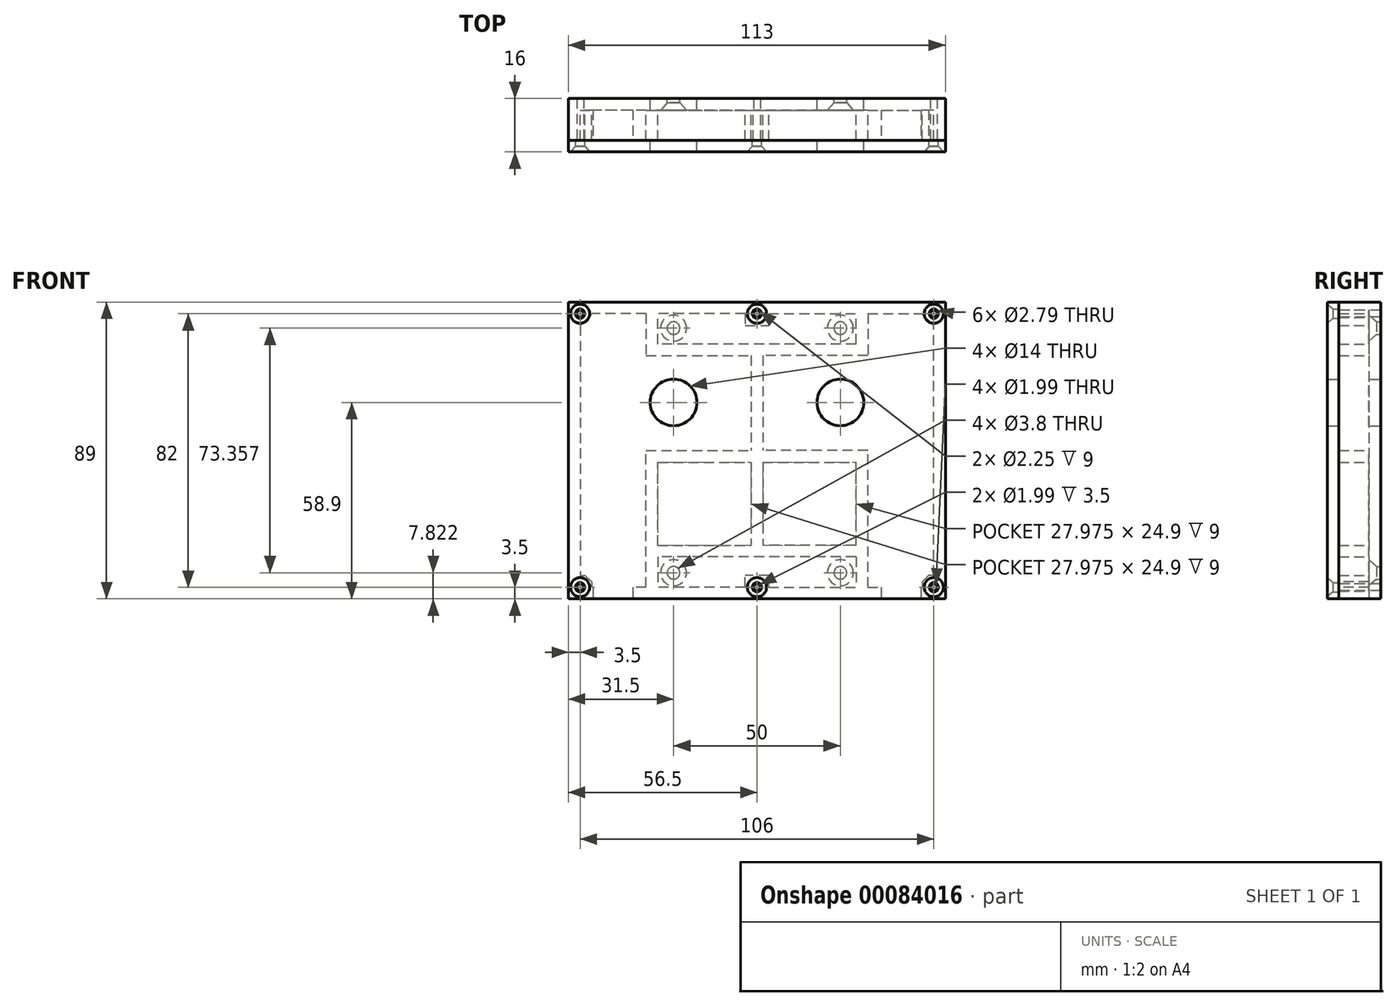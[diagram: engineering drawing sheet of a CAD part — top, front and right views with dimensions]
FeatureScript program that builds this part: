
annotation { "Feature Type Name" : "Feature", "Feature Type Description" : "" }
export const myFeature = defineFeature(function(context is Context, id is Id, definition is map)
    precondition{}
    {
        {
            var Q0;
            Q0=qCreatedBy(makeId("Front.planeOp"),FACE);
            var sketch = newSketch(context, id + "F0", { "sketchPlane" : qUnion([Q0])});
            skLineSegment(sketch, "E0.0", {"start": v(-53, 0) * mm, "end": v(-53, 37.41) * mm});
            skLineSegment(sketch, "E1.trimOffspring", {"start": v(-29.73, 31.9) * mm, "end": v(-29.73, 41) * mm});
            skLineSegment(sketch, "E2.0", {"start": v(0, 31.9) * mm, "end": v(-29.73, 31.9) * mm});
            skLineSegment(sketch, "E3.trimOffspring", {"start": v(-33.23, 41) * mm, "end": v(-49.5, 41) * mm});
            skLineSegment(sketch, "E4.trimOffspring", {"start": v(-3.5, 41) * mm, "end": v(-29.73, 41) * mm});
            skLineSegment(sketch, "E5.MirrorCS", {"start": v(-3.5, 41) * mm, "end": v(-3.5, 37.5) * mm});
            skLineSegment(sketch, "E6", {"start": v(-3.5, 37.5) * mm, "end": v(0, 37.5) * mm});
            skCircle(sketch, "E7", {"center": v(-25, 14.4) * mm, "radius": 7 * mm});
            skCircle(sketch, "E8", {"center": v(-53, 41) * mm, "radius": 0.5 * mm});
            skLineSegment(sketch, "E9", {"start": v(-56.5, 44.5) * mm, "end": v(-56.5, 0) * mm});
            skLineSegment(sketch, "E10", {"start": v(-56.5, 44.5) * mm, "end": v(0, 44.5) * mm});
            skLineSegment(sketch, "E11", {"start": v(-53, 37.41) * mm, "end": v(-49.5, 41) * mm});
            skLineSegment(sketch, "E12", {"start": v(0, 89.77) * mm, "end": v(0, -70.35) * mm, "construction": true});
            skLineSegment(sketch, "E13", {"start": v(-110.4, 0) * mm, "end": v(109.76, 0) * mm, "construction": true});
            skLineSegment(sketch, "E14", {"start": v(-33.23, 28.4) * mm, "end": v(0, 28.4) * mm});
            skLineSegment(sketch, "E15.MirrorCS", {"start": v(56.5, 44.5) * mm, "end": v(0, 44.5) * mm});
            skLineSegment(sketch, "E16.MirrorCS", {"start": v(56.5, 44.5) * mm, "end": v(56.5, 0) * mm});
            skLineSegment(sketch, "E17.MirrorCS", {"start": v(-56.5, -44.5) * mm, "end": v(-56.5, 0) * mm});
            skLineSegment(sketch, "E18.MirrorCS", {"start": v(-56.5, -44.5) * mm, "end": v(0, -44.5) * mm});
            skLineSegment(sketch, "E19.MirrorCS", {"start": v(56.5, -44.5) * mm, "end": v(0, -44.5) * mm});
            skLineSegment(sketch, "E20.MirrorCS", {"start": v(56.5, -44.5) * mm, "end": v(56.5, 0) * mm});
            skLineSegment(sketch, "E21.MirrorCS", {"start": v(33.23, 28.4) * mm, "end": v(0, 28.4) * mm});
            skLineSegment(sketch, "E22.MirrorCS", {"start": v(0, 31.9) * mm, "end": v(29.73, 31.9) * mm});
            skLineSegment(sketch, "E23.MirrorCS", {"start": v(33.23, 41) * mm, "end": v(33.23, 28.4) * mm});
            skLineSegment(sketch, "E24.MirrorCS", {"start": v(29.73, 31.9) * mm, "end": v(29.73, 41) * mm});
            skLineSegment(sketch, "E25.MirrorCS", {"start": v(3.5, 41) * mm, "end": v(29.73, 41) * mm});
            skLineSegment(sketch, "E26.MirrorCS", {"start": v(33.23, 41) * mm, "end": v(49.5, 41) * mm});
            skLineSegment(sketch, "E27.MirrorCS", {"start": v(53, 37.41) * mm, "end": v(49.5, 41) * mm});
            skLineSegment(sketch, "E28.MirrorCS", {"start": v(53, 0) * mm, "end": v(53, 37.41) * mm});
            skCircle(sketch, "E29.MirrorC", {"center": v(25, 14.4) * mm, "radius": 7 * mm});
            skCircle(sketch, "E30.MirrorC", {"center": v(53, 41) * mm, "radius": 0.5 * mm});
            skLineSegment(sketch, "E31.MirrorCS", {"start": v(53, 0) * mm, "end": v(53, -37.41) * mm});
            skCircle(sketch, "E32.MirrorC", {"center": v(53, -41) * mm, "radius": 0.5 * mm});
            skLineSegment(sketch, "E33.MirrorCS", {"start": v(33.23, -41) * mm, "end": v(49.5, -41) * mm});
            skLineSegment(sketch, "E34.MirrorCS", {"start": v(29.73, -28.4) * mm, "end": v(0, -28.4) * mm});
            skLineSegment(sketch, "E35.MirrorCS", {"start": v(0, -31.9) * mm, "end": v(29.73, -31.9) * mm});
            skLineSegment(sketch, "E36.MirrorCS", {"start": v(29.73, -31.9) * mm, "end": v(29.73, -41) * mm});
            skLineSegment(sketch, "E37.MirrorCS", {"start": v(3.5, -41) * mm, "end": v(29.73, -41) * mm});
            skLineSegment(sketch, "E38.MirrorCS", {"start": v(3.5, 41) * mm, "end": v(3.5, 37.5) * mm});
            skLineSegment(sketch, "E39.MirrorCS", {"start": v(3.5, 37.5) * mm, "end": v(0, 37.5) * mm});
            skLineSegment(sketch, "E40.MirrorCS", {"start": v(3.5, -41) * mm, "end": v(3.5, -37.5) * mm});
            skLineSegment(sketch, "E41.MirrorCS", {"start": v(3.5, -37.5) * mm, "end": v(0, -37.5) * mm});
            skLineSegment(sketch, "E42.MirrorCS", {"start": v(-3.5, -37.5) * mm, "end": v(0, -37.5) * mm});
            skLineSegment(sketch, "E43.MirrorCS", {"start": v(-3.5, -41) * mm, "end": v(-3.5, -37.5) * mm});
            skLineSegment(sketch, "E44.MirrorCS", {"start": v(-3.5, -41) * mm, "end": v(-29.73, -41) * mm});
            skLineSegment(sketch, "E45.MirrorCS", {"start": v(-29.73, -31.9) * mm, "end": v(-29.73, -41) * mm});
            skLineSegment(sketch, "E46.MirrorCS", {"start": v(0, -31.9) * mm, "end": v(-29.73, -31.9) * mm});
            skLineSegment(sketch, "E47.MirrorCS", {"start": v(-29.73, -28.4) * mm, "end": v(0, -28.4) * mm});
            skLineSegment(sketch, "E48.MirrorCS", {"start": v(-33.23, -41) * mm, "end": v(-49.5, -41) * mm});
            skLineSegment(sketch, "E49.MirrorCS", {"start": v(-53, 0) * mm, "end": v(-53, -37.41) * mm});
            skCircle(sketch, "E50.MirrorC", {"center": v(-53, -41) * mm, "radius": 0.5 * mm});
            skCircle(sketch, "E51", {"center": v(0, 41) * mm, "radius": 1.13 * mm});
            skCircle(sketch, "E52.MirrorC", {"center": v(0, -41) * mm, "radius": 1.13 * mm});
            skLineSegment(sketch, "E53", {"start": v(-1.75, 28.4) * mm, "end": v(-1.75, -28.4) * mm});
            skLineSegment(sketch, "E54.MirrorCS", {"start": v(1.75, 28.4) * mm, "end": v(1.75, -28.4) * mm});
            skLineSegment(sketch, "E55.left", {"start": v(-29.73, -28.4) * mm, "end": v(-29.73, -3.5) * mm});
            skLineSegment(sketch, "E55.right", {"start": v(-33.23, -41) * mm, "end": v(-33.23, 0) * mm});
            skLineSegment(sketch, "E56.MirrorCS", {"start": v(29.73, -28.4) * mm, "end": v(29.73, -3.5) * mm});
            skLineSegment(sketch, "E57.top", {"start": v(-29.73, -3.5) * mm, "end": v(29.73, -3.5) * mm});
            skLineSegment(sketch, "E58", {"start": v(-33.23, 41) * mm, "end": v(-33.23, 28.4) * mm});
            skLineSegment(sketch, "E59", {"start": v(-53, -37.41) * mm, "end": v(-49.5, -37.41) * mm});
            skLineSegment(sketch, "E60", {"start": v(-49.5, -37.41) * mm, "end": v(-49.5, -41) * mm});
            skLineSegment(sketch, "E61.MirrorCS", {"start": v(53, -37.41) * mm, "end": v(49.5, -37.41) * mm});
            skLineSegment(sketch, "E62.MirrorCS", {"start": v(49.5, -37.41) * mm, "end": v(49.5, -41) * mm});
            skCircle(sketch, "E63", {"center": v(-25, 36.68) * mm, "radius": 0.5 * mm});
            skCircle(sketch, "E64.MirrorC", {"center": v(25, 36.68) * mm, "radius": 0.5 * mm});
            skCircle(sketch, "E65.MirrorC", {"center": v(-25, -36.68) * mm, "radius": 0.5 * mm});
            skLineSegment(sketch, "E66.MirrorCS", {"start": v(33.23, -41) * mm, "end": v(33.23, 0) * mm});
            skLineSegment(sketch, "E67", {"start": v(-33.23, 0) * mm, "end": v(0, 0) * mm});
            skLineSegment(sketch, "E68.MirrorCS", {"start": v(33.23, 0) * mm, "end": v(0, 0) * mm});
            skCircle(sketch, "E69.MirrorC", {"center": v(25, -36.68) * mm, "radius": 0.5 * mm});
            skSolve(sketch);
        }
        {
            var Q0;
            {var subQ17=sQuery(id+"F0.wireOp",EDGE,"E0.0");Q0=makeQuery(id+"F0.imprint","IMPRINT",FACE,{"disambiguationData":[TD([[makeQuery(id+"F0.imprint","IMPRINT",EDGE,{"derivedFrom":subQ17}),1.0]])]});}
            var Q1;
            {var subQ1=sQuery(id+"F0.wireOp",EDGE,"E21.MirrorCS");var subQ6=sQuery(id+"F0.wireOp",EDGE,"E14");var subQ9=makeQuery(id+"F0.imprint","INTERSECT",VERTEX,{"derivedFrom":[subQ6,subQ1]});Q1=makeQuery(id+"F0.imprint","IMPRINT",FACE,{"disambiguationData":[TD([[makeQuery(id+"F0.imprint","IMPRINT",EDGE,{"disambiguationData":[TD([[subQ9,1.0]])],"derivedFrom":subQ6}),-1.0]])]});}
            var Q2;
            {var subQ0=sQuery(id+"F0.wireOp",EDGE,"E57.bottom");var subQ1=sQuery(id+"F0.wireOp",EDGE,"E53");var subQ2=makeQuery(id+"F0.imprint","INTERSECT",VERTEX,{"derivedFrom":[subQ1,subQ0]});Q2=makeQuery(id+"F0.imprint","IMPRINT",FACE,{"disambiguationData":[TD([[makeQuery(id+"F0.imprint","IMPRINT",EDGE,{"disambiguationData":[TD([[subQ2,-1.0]])],"derivedFrom":subQ1}),1.0]])]});}
            var Q3;
            {var subQ1=sQuery(id+"F0.wireOp",EDGE,"E47.MirrorCS");var subQ6=sQuery(id+"F0.wireOp",EDGE,"E34.MirrorCS");var subQ9=makeQuery(id+"F0.imprint","INTERSECT",VERTEX,{"derivedFrom":[subQ6,subQ1]});Q3=makeQuery(id+"F0.imprint","IMPRINT",FACE,{"disambiguationData":[TD([[makeQuery(id+"F0.imprint","IMPRINT",EDGE,{"disambiguationData":[TD([[subQ9,1.0]])],"derivedFrom":subQ6}),-1.0]])]});}
            extrude(context, id + "F1", {"entities" : qUnion([Q0, Q1, Q2, Q3]), "depth" : 12.5 * mm});
        }
        {
            var Q0;
            {var subQ3=sQuery(id+"F0.wireOp",EDGE,"E0.0");Q0=makeQuery(id+"F0.imprint","IMPRINT",FACE,{"disambiguationData":[TD([[makeQuery(id+"F0.imprint","IMPRINT",EDGE,{"derivedFrom":subQ3}),-1.0]])]});}
            var Q1;
            Q1=makeQuery(id+"F0.imprint","IMPRINT",FACE,{"disambiguationData":[TD([[makeQuery(id+"F0.imprint","IMPRINT",EDGE,{"derivedFrom":sQuery(id+"F0.wireOp",EDGE,"E1.trimOffspring")}),-1.0]])]});
            var Q2;
            {var subQ8=sQuery(id+"F0.wireOp",EDGE,"E23.MirrorCS");Q2=makeQuery(id+"F0.imprint","IMPRINT",FACE,{"disambiguationData":[TD([[makeQuery(id+"F0.imprint","IMPRINT",EDGE,{"derivedFrom":subQ8}),1.0]])]});}
            var Q3;
            {var subQ0=sQuery(id+"F0.wireOp",EDGE,"E56.MirrorCS");Q3=makeQuery(id+"F0.imprint","IMPRINT",FACE,{"disambiguationData":[TD([[makeQuery(id+"F0.imprint","IMPRINT",EDGE,{"derivedFrom":subQ0}),1.0]])]});}
            var Q4;
            Q4=makeQuery(id+"F0.imprint","IMPRINT",FACE,{"disambiguationData":[TD([[makeQuery(id+"F0.imprint","IMPRINT",EDGE,{"derivedFrom":sQuery(id+"F0.wireOp",EDGE,"E35.MirrorCS")}),-1.0]])]});
            var Q5;
            {var subQ0=sQuery(id+"F0.wireOp",EDGE,"E55.left");Q5=makeQuery(id+"F0.imprint","IMPRINT",FACE,{"disambiguationData":[TD([[makeQuery(id+"F0.imprint","IMPRINT",EDGE,{"derivedFrom":subQ0}),-1.0]])]});}
            extrude(context, id + "F2", {"entities" : qUnion([Q0, Q1, Q2, Q3, Q4, Q5]), "operationType" : NewBodyOperationType.ADD, "depth" : 3.5 * mm});
        }
        {
            var Q0;
            Q0=makeQuery(id+"F1.opExtrude","SWEPT_FACE",FACE,{"disambiguationData":[OSD([sQuery(id+"F0.wireOp",EDGE,"E18.MirrorCS"),sQuery(id+"F0.wireOp",EDGE,"E19.MirrorCS")])]});
            var sketch = newSketch(context, id + "F3", { "sketchPlane" : qUnion([Q0])});
            skLineSegment(sketch, "E70.bottom", {"start": v(-37.25, 3.5) * mm, "end": v(-49.15, 3.5) * mm});
            skLineSegment(sketch, "E70.left", {"start": v(-37.25, 3.5) * mm, "end": v(-37.25, 12.5) * mm});
            skLineSegment(sketch, "E70.right", {"start": v(-49.15, 3.5) * mm, "end": v(-49.15, 12.5) * mm});
            skPoint(sketch, "E70.middle", {"position": v(-43.2, 6.25) * mm});
            skPoint(sketch, "E70.middle.positionSnap0", {"position": v(-56.5, 6.25) * mm});
            skPoint(sketch, "E70.centerSnap0", {"position": v(-56.5, 6.25) * mm});
            skLineSegment(sketch, "E71", {"start": v(-49.15, 12.5) * mm, "end": v(-37.25, 12.5) * mm});
            skLineSegment(sketch, "E72.MirrorCS", {"start": v(49.15, 12.5) * mm, "end": v(37.25, 12.5) * mm});
            skLineSegment(sketch, "E73.MirrorCS", {"start": v(37.25, 3.5) * mm, "end": v(37.25, 12.5) * mm});
            skLineSegment(sketch, "E74.MirrorCS", {"start": v(49.15, 3.5) * mm, "end": v(49.15, 12.5) * mm});
            skLineSegment(sketch, "E75.MirrorCS", {"start": v(37.25, 3.5) * mm, "end": v(49.15, 3.5) * mm});
            skSolve(sketch);
        }
        {
            var Q0;
            Q0=makeQuery(id+"F3.imprint","IMPRINT",FACE,{"disambiguationData":[TD([[makeQuery(id+"F3.imprint","IMPRINT",EDGE,{"derivedFrom":sQuery(id+"F3.wireOp",EDGE,"E70.bottom")}),-1.0]])]});
            var Q1;
            Q1=makeQuery(id+"F3.imprint","IMPRINT",FACE,{"disambiguationData":[TD([[makeQuery(id+"F3.imprint","IMPRINT",EDGE,{"derivedFrom":sQuery(id+"F3.wireOp",EDGE,"E72.MirrorCS")}),-1.0]])]});
            extrude(context, id + "F4", {"entities" : qUnion([Q0, Q1]), "operationType" : NewBodyOperationType.REMOVE, "oppositeDirection" : true, "depth" : 19.49 * mm});
        }
        {
            var Q0;
            Q0=qCreatedBy(makeId("Front.planeOp"),FACE);
            var sketch = newSketch(context, id + "F5", { "sketchPlane" : qUnion([Q0])});
            skLineSegment(sketch, "E76.0.2", {"start": v(49.15, -44.5) * mm, "end": v(56.5, -44.5) * mm});
            skLineSegment(sketch, "E76.0.3", {"start": v(56.5, -44.5) * mm, "end": v(56.5, 44.5) * mm});
            skLineSegment(sketch, "E76.0.4", {"start": v(56.5, 44.5) * mm, "end": v(-56.5, 44.5) * mm});
            skLineSegment(sketch, "E76.0.5", {"start": v(-56.5, 44.5) * mm, "end": v(-56.5, -44.5) * mm});
            skLineSegment(sketch, "E76.0.6", {"start": v(-56.5, -44.5) * mm, "end": v(-49.15, -44.5) * mm});
            skLineSegment(sketch, "E76.0.20", {"start": v(-37.25, -44.5) * mm, "end": v(37.25, -44.5) * mm});
            skCircle(sketch, "E77.0", {"center": v(-53, 41) * mm, "radius": 0.5 * mm});
            skCircle(sketch, "E78.0", {"center": v(0, 41) * mm, "radius": 1.13 * mm});
            skCircle(sketch, "E79.0", {"center": v(53, 41) * mm, "radius": 0.5 * mm});
            skCircle(sketch, "E80.0", {"center": v(53, -41) * mm, "radius": 0.5 * mm});
            skCircle(sketch, "E81.0", {"center": v(0, -41) * mm, "radius": 1.13 * mm});
            skCircle(sketch, "E82.0", {"center": v(-53, -41) * mm, "radius": 0.5 * mm});
            skLineSegment(sketch, "E83", {"start": v(-49.15, -44.5) * mm, "end": v(-37.25, -44.5) * mm});
            skLineSegment(sketch, "E84", {"start": v(37.25, -44.5) * mm, "end": v(49.15, -44.5) * mm});
            skCircle(sketch, "E85.0", {"center": v(-25, 14.4) * mm, "radius": 7 * mm});
            skCircle(sketch, "E86.0", {"center": v(25, 14.4) * mm, "radius": 7 * mm});
            skSolve(sketch);
        }
        {
            var Q0;
            Q0 = qSketchRegion(id + "F5", true);
            extrude(context, id + "F6", {"entities" : qUnion([Q0]), "depth" : 3.5 * mm});
        }
        {
            var Q0;
            Q0=makeQuery(id+"F6.opExtrude","CAP_FACE",FACE,{"disambiguationData":[OSD([sQuery(id+"F5.wireOp",EDGE,"E76.0.2"),sQuery(id+"F5.wireOp",EDGE,"E76.0.3"),sQuery(id+"F5.wireOp",EDGE,"E76.0.4"),sQuery(id+"F5.wireOp",EDGE,"E76.0.5"),sQuery(id+"F5.wireOp",EDGE,"E76.0.6"),sQuery(id+"F5.wireOp",EDGE,"E76.0.20"),sQuery(id+"F5.wireOp",EDGE,"E77.0"),sQuery(id+"F5.wireOp",EDGE,"E78.0"),sQuery(id+"F5.wireOp",EDGE,"E79.0"),sQuery(id+"F5.wireOp",EDGE,"E80.0"),sQuery(id+"F5.wireOp",EDGE,"E81.0"),sQuery(id+"F5.wireOp",EDGE,"E82.0"),sQuery(id+"F5.wireOp",EDGE,"E83"),sQuery(id+"F5.wireOp",EDGE,"E84"),sQuery(id+"F5.wireOp",EDGE,"E85.0"),sQuery(id+"F5.wireOp",EDGE,"E86.0")])],"isStart":false});
            var sketch = newSketch(context, id + "F7", { "sketchPlane" : qUnion([Q0])});
            skCircle(sketch, "E87.0", {"center": v(-53, 41) * mm, "radius": 0.5 * mm});
            skCircle(sketch, "E88.0", {"center": v(0, 41) * mm, "radius": 1.13 * mm});
            skCircle(sketch, "E89.0", {"center": v(53, 41) * mm, "radius": 0.5 * mm});
            skCircle(sketch, "E90.0", {"center": v(53, -41) * mm, "radius": 0.5 * mm});
            skCircle(sketch, "E91.0", {"center": v(0, -41) * mm, "radius": 1.13 * mm});
            skCircle(sketch, "E92.0", {"center": v(-53, -41) * mm, "radius": 0.5 * mm});
            skSolve(sketch);
        }
        {
            var Q0;
            Q0=sQuery(id+"F7.wireOp",VERTEX,"E87.0.center");
            var Q1;
            Q1=sQuery(id+"F7.wireOp",VERTEX,"E88.0.center");
            var Q2;
            Q2=sQuery(id+"F7.wireOp",VERTEX,"E89.0.center");
            var Q3;
            Q3=sQuery(id+"F7.wireOp",VERTEX,"E90.0.center");
            var Q4;
            Q4=sQuery(id+"F7.wireOp",VERTEX,"E91.0.center");
            var Q5;
            Q5=sQuery(id+"F7.wireOp",VERTEX,"E92.0.center");
            var Q6;
            Q6=makeQuery(id+"F6.opExtrude","SWEPT_BODY",BODY,{"disambiguationData":[OSD([sQuery(id+"F5.wireOp",EDGE,"E76.0.2"),sQuery(id+"F5.wireOp",EDGE,"E76.0.3"),sQuery(id+"F5.wireOp",EDGE,"E76.0.4"),sQuery(id+"F5.wireOp",EDGE,"E76.0.5"),sQuery(id+"F5.wireOp",EDGE,"E76.0.6"),sQuery(id+"F5.wireOp",EDGE,"E76.0.20"),sQuery(id+"F5.wireOp",EDGE,"E77.0"),sQuery(id+"F5.wireOp",EDGE,"E78.0"),sQuery(id+"F5.wireOp",EDGE,"E79.0"),sQuery(id+"F5.wireOp",EDGE,"E80.0"),sQuery(id+"F5.wireOp",EDGE,"E81.0"),sQuery(id+"F5.wireOp",EDGE,"E82.0"),sQuery(id+"F5.wireOp",EDGE,"E83"),sQuery(id+"F5.wireOp",EDGE,"E84"),sQuery(id+"F5.wireOp",EDGE,"E85.0"),sQuery(id+"F5.wireOp",EDGE,"E86.0")])]});
            hole(context, id + "F8", {"style" : HoleStyle.C_SINK, "endStyle" : HoleEndStyle.THROUGH, "standardTappedOrClearance" : lookupTablePath({ "standard" : "ANSI", "fit" : "Normal (ASME)", "size" : "#3", "type" : "Clearance" }), "standardBlindInLast" : lookupTablePath({ "fit" : "Free", "standard" : "ANSI", "size" : "#3", "type" : "Clearance" }), "holeDiameter" : 2.8 * mm, "cSinkDiameter" : 5.74 * mm, "cSinkAngle" : 82 * degree, "locations" : qUnion([Q0, Q1, Q2, Q3, Q4, Q5]), "scope" : qUnion([Q6]), "isTappedThrough" : true, "startStyle" : HoleStartStyle.PART});
        }
        {
            var Q0;
            Q0=makeQuery(id+"F6.opExtrude","SWEPT_BODY",BODY,{"disambiguationData":[OSD([sQuery(id+"F5.wireOp",EDGE,"E76.0.2"),sQuery(id+"F5.wireOp",EDGE,"E76.0.3"),sQuery(id+"F5.wireOp",EDGE,"E76.0.4"),sQuery(id+"F5.wireOp",EDGE,"E76.0.5"),sQuery(id+"F5.wireOp",EDGE,"E76.0.6"),sQuery(id+"F5.wireOp",EDGE,"E76.0.20"),sQuery(id+"F5.wireOp",EDGE,"E77.0"),sQuery(id+"F5.wireOp",EDGE,"E78.0"),sQuery(id+"F5.wireOp",EDGE,"E79.0"),sQuery(id+"F5.wireOp",EDGE,"E80.0"),sQuery(id+"F5.wireOp",EDGE,"E81.0"),sQuery(id+"F5.wireOp",EDGE,"E82.0"),sQuery(id+"F5.wireOp",EDGE,"E83"),sQuery(id+"F5.wireOp",EDGE,"E84")])]});
            transform(context, id + "F9", {"entities" : qUnion([Q0]), "transformType" : TransformType.TRANSLATION_3D, "dx" : 0 * mm, "dy" : -12.5 * mm, "dz" : 0 * mm, "makeCopy" : false});
        }
        {
            var Q0;
            {var subQ0=sQuery(id+"F0.wireOp",EDGE,"E57.top");var subQ1=sQuery(id+"F0.wireOp",EDGE,"E55.left");var subQ2=sQuery(id+"F0.wireOp",EDGE,"E53");var subQ3=sQuery(id+"F0.wireOp",EDGE,"E47.MirrorCS");var subQ4=sQuery(id+"F0.wireOp",EDGE,"E46.MirrorCS");var subQ5=sQuery(id+"F0.wireOp",EDGE,"E45.MirrorCS");var subQ6=sQuery(id+"F0.wireOp",EDGE,"E44.MirrorCS");var subQ7=sQuery(id+"F0.wireOp",EDGE,"E43.MirrorCS");var subQ8=sQuery(id+"F0.wireOp",EDGE,"E42.MirrorCS");var subQ9=sQuery(id+"F0.wireOp",EDGE,"E41.MirrorCS");var subQ10=sQuery(id+"F0.wireOp",EDGE,"E40.MirrorCS");var subQ11=sQuery(id+"F0.wireOp",EDGE,"E37.MirrorCS");var subQ12=sQuery(id+"F0.wireOp",EDGE,"E36.MirrorCS");var subQ13=sQuery(id+"F0.wireOp",EDGE,"E35.MirrorCS");var subQ14=sQuery(id+"F0.wireOp",EDGE,"E56.MirrorCS");var subQ15=sQuery(id+"F0.wireOp",EDGE,"E54.MirrorCS");var subQ16=sQuery(id+"F0.wireOp",EDGE,"E34.MirrorCS");var subQ17=sQuery(id+"F0.wireOp",EDGE,"E62.MirrorCS");var subQ18=sQuery(id+"F0.wireOp",EDGE,"E61.MirrorCS");var subQ19=sQuery(id+"F0.wireOp",EDGE,"13d9dcca-07fb-4331-a37f-d2f940aab7110.MirrorCS");var subQ20=sQuery(id+"F0.wireOp",EDGE,"1773fa3a-ab13-4435-ac9a-09cd98a18d640.MirrorCS");var subQ21=sQuery(id+"F0.wireOp",EDGE,"E57.bottom");var subQ22=sQuery(id+"F0.wireOp",EDGE,"E33.MirrorCS");var subQ23=sQuery(id+"F0.wireOp",EDGE,"E31.MirrorCS");var subQ24=sQuery(id+"F0.wireOp",EDGE,"E28.MirrorCS");var subQ25=sQuery(id+"F0.wireOp",EDGE,"E27.MirrorCS");var subQ26=sQuery(id+"F0.wireOp",EDGE,"E26.MirrorCS");var subQ27=sQuery(id+"F0.wireOp",EDGE,"E23.MirrorCS");var subQ28=sQuery(id+"F0.wireOp",EDGE,"E21.MirrorCS");var subQ29=sQuery(id+"F0.wireOp",EDGE,"E39.MirrorCS");var subQ30=sQuery(id+"F0.wireOp",EDGE,"E38.MirrorCS");var subQ31=sQuery(id+"F0.wireOp",EDGE,"E25.MirrorCS");var subQ32=sQuery(id+"F0.wireOp",EDGE,"E24.MirrorCS");var subQ33=sQuery(id+"F0.wireOp",EDGE,"E22.MirrorCS");var subQ34=sQuery(id+"F0.wireOp",EDGE,"E6");var subQ35=sQuery(id+"F0.wireOp",EDGE,"E5.MirrorCS");var subQ36=sQuery(id+"F0.wireOp",EDGE,"E4.trimOffspring");var subQ37=sQuery(id+"F0.wireOp",EDGE,"E2.0");var subQ38=sQuery(id+"F0.wireOp",EDGE,"E1.trimOffspring");var subQ39=sQuery(id+"F0.wireOp",EDGE,"E60");var subQ40=sQuery(id+"F0.wireOp",EDGE,"E59");var subQ41=sQuery(id+"F0.wireOp",EDGE,"E58");var subQ42=sQuery(id+"F0.wireOp",EDGE,"E57.left");var subQ43=sQuery(id+"F0.wireOp",EDGE,"E55.right");var subQ44=sQuery(id+"F0.wireOp",EDGE,"E49.MirrorCS");var subQ45=sQuery(id+"F0.wireOp",EDGE,"E48.MirrorCS");var subQ46=sQuery(id+"F0.wireOp",EDGE,"0d077449-7af7-4c96-af97-3517e80e3f0b0.MirrorCS");var subQ47=sQuery(id+"F0.wireOp",EDGE,"E14");var subQ48=sQuery(id+"F0.wireOp",EDGE,"E11");var subQ49=sQuery(id+"F0.wireOp",EDGE,"E3.trimOffspring");var subQ50=sQuery(id+"F0.wireOp",EDGE,"E0.0");Q0=makeQuery(id+"F2.boolean.opBoolean","MERGE",FACE,{"derivedFrom":[makeQuery(id+"F1.opExtrude","CAP_FACE",FACE,{"disambiguationData":[OSD([subQ50,subQ38,subQ37,subQ49,subQ36,subQ35,subQ34,sQuery(id+"F0.wireOp",EDGE,"E8"),sQuery(id+"F0.wireOp",EDGE,"E9"),sQuery(id+"F0.wireOp",EDGE,"E10"),subQ48,subQ47,sQuery(id+"F0.wireOp",EDGE,"E15.MirrorCS"),sQuery(id+"F0.wireOp",EDGE,"E16.MirrorCS"),sQuery(id+"F0.wireOp",EDGE,"E17.MirrorCS"),sQuery(id+"F0.wireOp",EDGE,"E18.MirrorCS"),sQuery(id+"F0.wireOp",EDGE,"E19.MirrorCS"),sQuery(id+"F0.wireOp",EDGE,"E20.MirrorCS"),subQ28,subQ33,subQ27,subQ32,subQ31,subQ26,subQ25,subQ24,sQuery(id+"F0.wireOp",EDGE,"E30.MirrorC"),subQ23,sQuery(id+"F0.wireOp",EDGE,"E32.MirrorC"),subQ22,subQ16,subQ13,subQ12,subQ11,subQ30,subQ29,subQ10,subQ9,subQ8,subQ7,subQ6,subQ5,subQ4,subQ3,subQ46,subQ45,subQ44,sQuery(id+"F0.wireOp",EDGE,"E50.MirrorC"),sQuery(id+"F0.wireOp",EDGE,"E51"),sQuery(id+"F0.wireOp",EDGE,"E52.MirrorC"),subQ2,subQ15,subQ1,subQ43,subQ14,subQ21,subQ0,subQ42,subQ41,subQ20,subQ19,subQ40,subQ39,subQ18,subQ17])],"isStart":true}),makeQuery(id+"F2.opExtrude","CAP_FACE",FACE,{"disambiguationData":[OSD([subQ50,subQ49,sQuery(id+"F0.wireOp",EDGE,"E7"),subQ48,subQ47,subQ46,subQ45,subQ44,subQ2,subQ43,subQ21,subQ42,subQ41,subQ40,subQ39])],"isStart":true}),makeQuery(id+"F2.opExtrude","CAP_FACE",FACE,{"disambiguationData":[OSD([subQ38,subQ37,subQ36,subQ35,subQ34,subQ33,subQ32,subQ31,subQ30,subQ29])],"isStart":true}),makeQuery(id+"F2.opExtrude","CAP_FACE",FACE,{"disambiguationData":[OSD([subQ28,subQ27,subQ26,subQ25,subQ24,sQuery(id+"F0.wireOp",EDGE,"E29.MirrorC"),subQ23,subQ22,subQ15,subQ21,subQ20,subQ19,subQ18,subQ17])],"isStart":true}),makeQuery(id+"F2.opExtrude","CAP_FACE",FACE,{"disambiguationData":[OSD([subQ16,subQ15,subQ14,subQ0])],"isStart":true}),makeQuery(id+"F2.opExtrude","CAP_FACE",FACE,{"disambiguationData":[OSD([subQ13,subQ12,subQ11,subQ10,subQ9,subQ8,subQ7,subQ6,subQ5,subQ4])],"isStart":true}),makeQuery(id+"F2.opExtrude","CAP_FACE",FACE,{"disambiguationData":[OSD([subQ3,subQ2,subQ1,subQ0])],"isStart":true})]});}
            var sketch = newSketch(context, id + "F10", { "sketchPlane" : qUnion([Q0])});
            skCircle(sketch, "E93.0", {"center": v(-53, 41) * mm, "radius": 0.5 * mm});
            skCircle(sketch, "E94.0", {"center": v(0, 41) * mm, "radius": 1.13 * mm});
            skCircle(sketch, "E95.0", {"center": v(53, 41) * mm, "radius": 0.5 * mm});
            skCircle(sketch, "E96.0", {"center": v(53, -41) * mm, "radius": 0.5 * mm});
            skCircle(sketch, "E97.0", {"center": v(0, -41) * mm, "radius": 1.13 * mm});
            skCircle(sketch, "E98.0", {"center": v(-53, -41) * mm, "radius": 0.5 * mm});
            skSolve(sketch);
        }
        {
            var Q0;
            Q0 = qSketchRegion(id + "F10", true);
            extrude(context, id + "F11", {"entities" : qUnion([Q0]), "operationType" : NewBodyOperationType.ADD, "oppositeDirection" : true, "depth" : 3.5 * mm});
        }
        {
            var Q0;
            Q0=makeQuery(id+"F1.opExtrude","SWEPT_EDGE",EDGE,{"disambiguationData":[OSD([sQuery(id+"F0.wireOp",EDGE,"E61.MirrorCS"),sQuery(id+"F0.wireOp",EDGE,"E62.MirrorCS")])]});
            var Q1;
            Q1=makeQuery(id+"F1.opExtrude","SWEPT_EDGE",EDGE,{"disambiguationData":[OSD([sQuery(id+"F0.wireOp",EDGE,"E59"),sQuery(id+"F0.wireOp",EDGE,"E60")])]});
            chamfer(context, id + "F12", {"entities" : qUnion([Q0, Q1]), "width" : 2 * mm, "tangentPropagation" : true});
        }
        {
            var Q0;
            Q0=sQuery(id+"F0.wireOp",VERTEX,"E8.center");
            var Q1;
            Q1=sQuery(id+"F0.wireOp",VERTEX,"E51.center");
            var Q2;
            Q2=sQuery(id+"F0.wireOp",VERTEX,"E30.MirrorC.center");
            var Q3;
            Q3=sQuery(id+"F0.wireOp",VERTEX,"E32.MirrorC.center");
            var Q4;
            Q4=sQuery(id+"F0.wireOp",VERTEX,"E52.MirrorC.center");
            var Q5;
            Q5=sQuery(id+"F0.wireOp",VERTEX,"E50.MirrorC.center");
            var Q6;
            Q6=makeQuery(id+"F1.opExtrude","SWEPT_BODY",BODY,{"disambiguationData":[OSD([sQuery(id+"F0.wireOp",EDGE,"E0.0"),sQuery(id+"F0.wireOp",EDGE,"E1.trimOffspring"),sQuery(id+"F0.wireOp",EDGE,"E2.0"),sQuery(id+"F0.wireOp",EDGE,"E3.trimOffspring"),sQuery(id+"F0.wireOp",EDGE,"E4.trimOffspring"),sQuery(id+"F0.wireOp",EDGE,"E5.MirrorCS"),sQuery(id+"F0.wireOp",EDGE,"E6"),sQuery(id+"F0.wireOp",EDGE,"E8"),sQuery(id+"F0.wireOp",EDGE,"E9"),sQuery(id+"F0.wireOp",EDGE,"E10"),sQuery(id+"F0.wireOp",EDGE,"E11"),sQuery(id+"F0.wireOp",EDGE,"E14"),sQuery(id+"F0.wireOp",EDGE,"E15.MirrorCS"),sQuery(id+"F0.wireOp",EDGE,"E16.MirrorCS"),sQuery(id+"F0.wireOp",EDGE,"E17.MirrorCS"),sQuery(id+"F0.wireOp",EDGE,"E18.MirrorCS"),sQuery(id+"F0.wireOp",EDGE,"E19.MirrorCS"),sQuery(id+"F0.wireOp",EDGE,"E20.MirrorCS"),sQuery(id+"F0.wireOp",EDGE,"E21.MirrorCS"),sQuery(id+"F0.wireOp",EDGE,"E22.MirrorCS"),sQuery(id+"F0.wireOp",EDGE,"E23.MirrorCS"),sQuery(id+"F0.wireOp",EDGE,"E24.MirrorCS"),sQuery(id+"F0.wireOp",EDGE,"E25.MirrorCS"),sQuery(id+"F0.wireOp",EDGE,"E26.MirrorCS"),sQuery(id+"F0.wireOp",EDGE,"E27.MirrorCS"),sQuery(id+"F0.wireOp",EDGE,"E28.MirrorCS"),sQuery(id+"F0.wireOp",EDGE,"E30.MirrorC"),sQuery(id+"F0.wireOp",EDGE,"E31.MirrorCS"),sQuery(id+"F0.wireOp",EDGE,"E32.MirrorC"),sQuery(id+"F0.wireOp",EDGE,"E33.MirrorCS"),sQuery(id+"F0.wireOp",EDGE,"E34.MirrorCS"),sQuery(id+"F0.wireOp",EDGE,"E35.MirrorCS"),sQuery(id+"F0.wireOp",EDGE,"E36.MirrorCS"),sQuery(id+"F0.wireOp",EDGE,"E37.MirrorCS"),sQuery(id+"F0.wireOp",EDGE,"E38.MirrorCS"),sQuery(id+"F0.wireOp",EDGE,"E39.MirrorCS"),sQuery(id+"F0.wireOp",EDGE,"E40.MirrorCS"),sQuery(id+"F0.wireOp",EDGE,"E41.MirrorCS"),sQuery(id+"F0.wireOp",EDGE,"E42.MirrorCS"),sQuery(id+"F0.wireOp",EDGE,"E43.MirrorCS"),sQuery(id+"F0.wireOp",EDGE,"E44.MirrorCS"),sQuery(id+"F0.wireOp",EDGE,"E45.MirrorCS"),sQuery(id+"F0.wireOp",EDGE,"E46.MirrorCS"),sQuery(id+"F0.wireOp",EDGE,"E47.MirrorCS"),sQuery(id+"F0.wireOp",EDGE,"E48.MirrorCS"),sQuery(id+"F0.wireOp",EDGE,"E49.MirrorCS"),sQuery(id+"F0.wireOp",EDGE,"E50.MirrorC"),sQuery(id+"F0.wireOp",EDGE,"E51"),sQuery(id+"F0.wireOp",EDGE,"E52.MirrorC"),sQuery(id+"F0.wireOp",EDGE,"E53"),sQuery(id+"F0.wireOp",EDGE,"E54.MirrorCS"),sQuery(id+"F0.wireOp",EDGE,"E55.left"),sQuery(id+"F0.wireOp",EDGE,"E55.right"),sQuery(id+"F0.wireOp",EDGE,"E56.MirrorCS"),sQuery(id+"F0.wireOp",EDGE,"E57.top"),sQuery(id+"F0.wireOp",EDGE,"E58"),sQuery(id+"F0.wireOp",EDGE,"E59"),sQuery(id+"F0.wireOp",EDGE,"E60"),sQuery(id+"F0.wireOp",EDGE,"E61.MirrorCS"),sQuery(id+"F0.wireOp",EDGE,"E62.MirrorCS"),sQuery(id+"F0.wireOp",EDGE,"E66.MirrorCS"),sQuery(id+"F0.wireOp",EDGE,"E67"),sQuery(id+"F0.wireOp",EDGE,"E68.MirrorCS")])]});
            hole(context, id + "F13", {"style" : HoleStyle.SIMPLE, "endStyle" : HoleEndStyle.THROUGH, "oppositeDirection" : true, "standardTappedOrClearance" : lookupTablePath({ "standard" : "ANSI", "engagement" : "75%", "pitch" : "48 tpi", "size" : "#3", "type" : "Tapped" }), "standardBlindInLast" : lookupTablePath({ "standard" : "ANSI", "engagement" : "75%", "pitch" : "48 tpi", "size" : "#3", "type" : "Tapped" }), "holeDiameter" : 2 * mm, "locations" : qUnion([Q0, Q1, Q2, Q3, Q4, Q5]), "scope" : qUnion([Q6]), "isTappedThrough" : true, "majorDiameter" : 2.5 * mm, "showTappedDepth" : true, "startStyle" : HoleStartStyle.PART});
        }
        {
            var Q0;
            Q0=makeQuery(id+"F2.opExtrude","CAP_FACE",FACE,{"disambiguationData":[OSD([sQuery(id+"F0.wireOp",EDGE,"E1.trimOffspring"),sQuery(id+"F0.wireOp",EDGE,"E2.0"),sQuery(id+"F0.wireOp",EDGE,"E4.trimOffspring"),sQuery(id+"F0.wireOp",EDGE,"E5.MirrorCS"),sQuery(id+"F0.wireOp",EDGE,"E6"),sQuery(id+"F0.wireOp",EDGE,"E22.MirrorCS"),sQuery(id+"F0.wireOp",EDGE,"E24.MirrorCS"),sQuery(id+"F0.wireOp",EDGE,"E25.MirrorCS"),sQuery(id+"F0.wireOp",EDGE,"E38.MirrorCS"),sQuery(id+"F0.wireOp",EDGE,"E39.MirrorCS"),sQuery(id+"F0.wireOp",EDGE,"E63"),sQuery(id+"F0.wireOp",EDGE,"E64.MirrorC")])],"isStart":false});
            var sketch = newSketch(context, id + "F14", { "sketchPlane" : qUnion([Q0])});
            skCircle(sketch, "E99.0", {"center": v(-25, 36.68) * mm, "radius": 0.5 * mm});
            skCircle(sketch, "E100.0", {"center": v(25, 36.68) * mm, "radius": 0.5 * mm});
            skCircle(sketch, "E101.0", {"center": v(-25, -36.68) * mm, "radius": 0.5 * mm});
            skCircle(sketch, "E102.0", {"center": v(25, -36.68) * mm, "radius": 0.5 * mm});
            skSolve(sketch);
        }
        {
            var Q0;
            Q0=sQuery(id+"F14.wireOp",VERTEX,"E99.0.center");
            var Q1;
            Q1=sQuery(id+"F14.wireOp",VERTEX,"E100.0.center");
            var Q2;
            Q2=sQuery(id+"F14.wireOp",VERTEX,"E102.0.center");
            var Q3;
            Q3=sQuery(id+"F14.wireOp",VERTEX,"E101.0.center");
            var Q4;
            Q4=makeQuery(id+"F1.opExtrude","SWEPT_BODY",BODY,{"disambiguationData":[OSD([sQuery(id+"F0.wireOp",EDGE,"E0.0"),sQuery(id+"F0.wireOp",EDGE,"E1.trimOffspring"),sQuery(id+"F0.wireOp",EDGE,"E2.0"),sQuery(id+"F0.wireOp",EDGE,"E3.trimOffspring"),sQuery(id+"F0.wireOp",EDGE,"E4.trimOffspring"),sQuery(id+"F0.wireOp",EDGE,"E5.MirrorCS"),sQuery(id+"F0.wireOp",EDGE,"E6"),sQuery(id+"F0.wireOp",EDGE,"E8"),sQuery(id+"F0.wireOp",EDGE,"E9"),sQuery(id+"F0.wireOp",EDGE,"E10"),sQuery(id+"F0.wireOp",EDGE,"E11"),sQuery(id+"F0.wireOp",EDGE,"E14"),sQuery(id+"F0.wireOp",EDGE,"E15.MirrorCS"),sQuery(id+"F0.wireOp",EDGE,"E16.MirrorCS"),sQuery(id+"F0.wireOp",EDGE,"E17.MirrorCS"),sQuery(id+"F0.wireOp",EDGE,"E18.MirrorCS"),sQuery(id+"F0.wireOp",EDGE,"E19.MirrorCS"),sQuery(id+"F0.wireOp",EDGE,"E20.MirrorCS"),sQuery(id+"F0.wireOp",EDGE,"E21.MirrorCS"),sQuery(id+"F0.wireOp",EDGE,"E22.MirrorCS"),sQuery(id+"F0.wireOp",EDGE,"E23.MirrorCS"),sQuery(id+"F0.wireOp",EDGE,"E24.MirrorCS"),sQuery(id+"F0.wireOp",EDGE,"E25.MirrorCS"),sQuery(id+"F0.wireOp",EDGE,"E26.MirrorCS"),sQuery(id+"F0.wireOp",EDGE,"E27.MirrorCS"),sQuery(id+"F0.wireOp",EDGE,"E28.MirrorCS"),sQuery(id+"F0.wireOp",EDGE,"E30.MirrorC"),sQuery(id+"F0.wireOp",EDGE,"E31.MirrorCS"),sQuery(id+"F0.wireOp",EDGE,"E32.MirrorC"),sQuery(id+"F0.wireOp",EDGE,"E33.MirrorCS"),sQuery(id+"F0.wireOp",EDGE,"E34.MirrorCS"),sQuery(id+"F0.wireOp",EDGE,"E35.MirrorCS"),sQuery(id+"F0.wireOp",EDGE,"E36.MirrorCS"),sQuery(id+"F0.wireOp",EDGE,"E37.MirrorCS"),sQuery(id+"F0.wireOp",EDGE,"E38.MirrorCS"),sQuery(id+"F0.wireOp",EDGE,"E39.MirrorCS"),sQuery(id+"F0.wireOp",EDGE,"E40.MirrorCS"),sQuery(id+"F0.wireOp",EDGE,"E41.MirrorCS"),sQuery(id+"F0.wireOp",EDGE,"E42.MirrorCS"),sQuery(id+"F0.wireOp",EDGE,"E43.MirrorCS"),sQuery(id+"F0.wireOp",EDGE,"E44.MirrorCS"),sQuery(id+"F0.wireOp",EDGE,"E45.MirrorCS"),sQuery(id+"F0.wireOp",EDGE,"E46.MirrorCS"),sQuery(id+"F0.wireOp",EDGE,"E47.MirrorCS"),sQuery(id+"F0.wireOp",EDGE,"E48.MirrorCS"),sQuery(id+"F0.wireOp",EDGE,"E49.MirrorCS"),sQuery(id+"F0.wireOp",EDGE,"E50.MirrorC"),sQuery(id+"F0.wireOp",EDGE,"E51"),sQuery(id+"F0.wireOp",EDGE,"E52.MirrorC"),sQuery(id+"F0.wireOp",EDGE,"E53"),sQuery(id+"F0.wireOp",EDGE,"E54.MirrorCS"),sQuery(id+"F0.wireOp",EDGE,"E55.left"),sQuery(id+"F0.wireOp",EDGE,"E55.right"),sQuery(id+"F0.wireOp",EDGE,"E56.MirrorCS"),sQuery(id+"F0.wireOp",EDGE,"E57.top"),sQuery(id+"F0.wireOp",EDGE,"E58"),sQuery(id+"F0.wireOp",EDGE,"E59"),sQuery(id+"F0.wireOp",EDGE,"E60"),sQuery(id+"F0.wireOp",EDGE,"E61.MirrorCS"),sQuery(id+"F0.wireOp",EDGE,"E62.MirrorCS"),sQuery(id+"F0.wireOp",EDGE,"E66.MirrorCS"),sQuery(id+"F0.wireOp",EDGE,"E67"),sQuery(id+"F0.wireOp",EDGE,"E68.MirrorCS")])]});
            hole(context, id + "F15", {"style" : HoleStyle.C_SINK, "endStyle" : HoleEndStyle.THROUGH, "standardTappedOrClearance" : lookupTablePath({ "standard" : "ANSI", "fit" : "Normal (ASME)", "size" : "#6", "type" : "Clearance" }), "standardBlindInLast" : lookupTablePath({ "fit" : "Free", "standard" : "ANSI", "size" : "#6", "type" : "Clearance" }), "holeDiameter" : 3.8 * mm, "cSinkDiameter" : 7.8 * mm, "cSinkAngle" : 82 * degree, "locations" : qUnion([Q0, Q1, Q2, Q3]), "scope" : qUnion([Q4]), "isTappedThrough" : true, "startStyle" : HoleStartStyle.PART});
        }
    });
